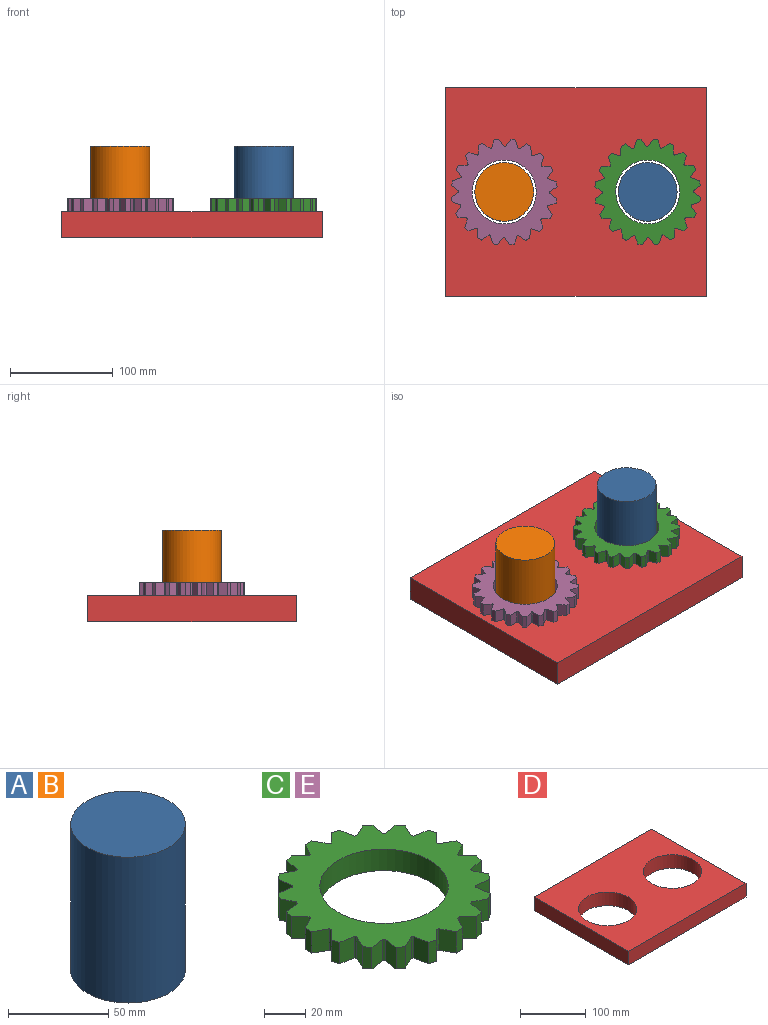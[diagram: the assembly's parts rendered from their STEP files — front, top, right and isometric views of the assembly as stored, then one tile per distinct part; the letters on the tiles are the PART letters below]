
ASSEMBLY  parts=5 mates=4
PART A: 3 faces, bbox 57.2x57.2x88.9 mm
  f0: cylinder r=28.57mm len=88.9mm, axis (0,0,-1), area 15961.3mm2, adj f1,f2
  f1: plane 57.15x57.15mm, normal (0,0,1), area 2565.2mm2, adj f0
  f2: plane 57.15x57.15mm, normal (0,0,-1), area 2565.2mm2, adj f0
PART B: same geometry as A
PART C: 83 faces, bbox 103.2x103.2x12.7 mm
  f0: plane 12.7x7.62mm, normal (0.47,0.88,0), area 109.7mm2, adj f1,f79,f81,f82
  f1: cylinder r=44.45mm len=12.7mm, axis (0,0,-1), area 15.5mm2, adj f0,f2,f81,f82
  f2: plane 12.7x6.21mm, normal (0.72,-0.69,0), area 109.6mm2, adj f1,f3,f81,f82
  f3: plane 12.7x4.35mm, normal (0.95,0.31,0), area 58.1mm2, adj f2,f4,f81,f82
  f4: plane 12.7x8.51mm, normal (0.18,0.98,0), area 109.7mm2, adj f3,f5,f81,f82
  f5: cylinder r=44.45mm len=12.7mm, axis (0,0,-1), area 15.5mm2, adj f4,f6,f81,f82
  f6: plane 12.7x7.76mm, normal (0.9,-0.44,0), area 109.6mm2, adj f5,f7,f81,f82
  f7: plane 12.7x3.7mm, normal (0.81,0.59,0), area 58.1mm2, adj f6,f8,f81,f82
  f8: plane 12.7x8.56mm, normal (-0.14,0.99,0), area 109.7mm2, adj f7,f9,f81,f82
  f9: cylinder r=44.45mm len=12.7mm, axis (0,0,-1), area 15.5mm2, adj f8,f10,f81,f82
  f10: plane 12.7x8.55mm, normal (0.99,-0.14,0), area 109.6mm2, adj f9,f11,f81,f82
  f11: plane 12.7x3.7mm, normal (0.59,0.81,0), area 58.1mm2, adj f10,f12,f81,f82
  f12: plane 12.7x7.77mm, normal (-0.44,0.9,0), area 109.7mm2, adj f11,f13,f81,f82
  f13: cylinder r=44.45mm len=12.7mm, axis (0,0,-1), area 15.5mm2, adj f12,f14,f81,f82
  f14: plane 12.7x8.5mm, normal (0.98,0.17,0), area 109.6mm2, adj f13,f15,f81,f82
  f15: plane 12.7x4.35mm, normal (0.31,0.95,0), area 58.1mm2, adj f14,f16,f81,f82
  f16: plane 12.7x6.23mm, normal (-0.69,0.72,0), area 109.7mm2, adj f15,f17,f81,f82
  f17: cylinder r=44.45mm len=12.7mm, axis (0,0,-1), area 15.5mm2, adj f16,f18,f81,f82
  f18: plane 12.7x7.62mm, normal (0.88,0.47,0), area 109.6mm2, adj f17,f19,f81,f82
  f19: plane 12.7x4.57mm, normal (0,1,0), area 58.1mm2, adj f18,f20,f81,f82
  f20: plane 12.7x7.62mm, normal (-0.88,0.47,0), area 109.7mm2, adj f19,f21,f81,f82
  f21: cylinder r=44.45mm len=12.7mm, axis (0,0,-1), area 15.5mm2, adj f20,f22,f81,f82
  f22: plane 12.7x6.21mm, normal (0.69,0.72,0), area 109.6mm2, adj f21,f23,f81,f82
  f23: plane 12.7x4.35mm, normal (-0.31,0.95,0), area 58.1mm2, adj f22,f24,f81,f82
  f24: plane 12.7x8.51mm, normal (-0.98,0.18,0), area 109.7mm2, adj f23,f25,f81,f82
  f25: cylinder r=44.45mm len=12.7mm, axis (0,0,-1), area 15.5mm2, adj f24,f26,f81,f82
  f26: plane 12.7x7.76mm, normal (0.44,0.9,0), area 109.6mm2, adj f25,f27,f81,f82
  f27: plane 12.7x3.7mm, normal (-0.59,0.81,0), area 58.1mm2, adj f26,f28,f81,f82
  f28: plane 12.7x8.56mm, normal (-0.99,-0.14,0), area 109.7mm2, adj f27,f29,f81,f82
  f29: cylinder r=44.45mm len=12.7mm, axis (0,0,-1), area 15.5mm2, adj f28,f30,f81,f82
  f30: plane 12.7x8.55mm, normal (0.14,0.99,0), area 109.6mm2, adj f29,f31,f81,f82
  f31: plane 12.7x3.7mm, normal (-0.81,0.59,0), area 58.1mm2, adj f30,f32,f81,f82
  f32: plane 12.7x7.77mm, normal (-0.9,-0.44,0), area 109.7mm2, adj f31,f33,f81,f82
  f33: cylinder r=44.45mm len=12.7mm, axis (0,0,-1), area 15.5mm2, adj f32,f34,f81,f82
  f34: plane 12.7x8.5mm, normal (-0.17,0.98,0), area 109.6mm2, adj f33,f35,f81,f82
  f35: plane 12.7x4.35mm, normal (-0.95,0.31,0), area 58.1mm2, adj f34,f36,f81,f82
  f36: plane 12.7x6.23mm, normal (-0.72,-0.69,0), area 109.7mm2, adj f35,f37,f81,f82
  f37: cylinder r=44.45mm len=12.7mm, axis (0,0,-1), area 15.5mm2, adj f36,f38,f81,f82
  f38: plane 12.7x7.62mm, normal (-0.47,0.88,0), area 109.6mm2, adj f37,f39,f81,f82
  f39: plane 12.7x4.57mm, normal (-1,0,0), area 58.1mm2, adj f38,f40,f81,f82
  f40: plane 12.7x7.62mm, normal (-0.47,-0.88,0), area 109.7mm2, adj f39,f41,f81,f82
  f41: cylinder r=44.45mm len=12.7mm, axis (0,0,-1), area 15.5mm2, adj f40,f42,f81,f82
  f42: plane 12.7x6.21mm, normal (-0.72,0.69,0), area 109.6mm2, adj f41,f43,f81,f82
  f43: plane 12.7x4.35mm, normal (-0.95,-0.31,0), area 58.1mm2, adj f42,f44,f81,f82
  f44: plane 12.7x8.51mm, normal (-0.18,-0.98,0), area 109.7mm2, adj f43,f45,f81,f82
  f45: cylinder r=44.45mm len=12.7mm, axis (0,0,-1), area 15.5mm2, adj f44,f46,f81,f82
  f46: plane 12.7x7.76mm, normal (-0.9,0.44,0), area 109.6mm2, adj f45,f47,f81,f82
  f47: plane 12.7x3.7mm, normal (-0.81,-0.59,0), area 58.1mm2, adj f46,f48,f81,f82
  f48: plane 12.7x8.56mm, normal (0.14,-0.99,0), area 109.7mm2, adj f47,f49,f81,f82
  f49: cylinder r=44.45mm len=12.7mm, axis (0,0,-1), area 15.5mm2, adj f48,f50,f81,f82
  f50: plane 12.7x8.55mm, normal (-0.99,0.14,0), area 109.6mm2, adj f49,f51,f81,f82
  f51: plane 12.7x3.7mm, normal (-0.59,-0.81,0), area 58.1mm2, adj f50,f52,f81,f82
  f52: plane 12.7x7.77mm, normal (0.44,-0.9,0), area 109.7mm2, adj f51,f53,f81,f82
  f53: cylinder r=44.45mm len=12.7mm, axis (0,0,-1), area 15.5mm2, adj f52,f54,f81,f82
  f54: plane 12.7x8.5mm, normal (-0.98,-0.17,0), area 109.6mm2, adj f53,f55,f81,f82
  f55: plane 12.7x4.35mm, normal (-0.31,-0.95,0), area 58.1mm2, adj f54,f56,f81,f82
  f56: plane 12.7x6.23mm, normal (0.69,-0.72,0), area 109.7mm2, adj f55,f57,f81,f82
  f57: cylinder r=44.45mm len=12.7mm, axis (0,0,-1), area 15.5mm2, adj f56,f58,f81,f82
  f58: plane 12.7x7.62mm, normal (-0.88,-0.47,0), area 109.6mm2, adj f57,f59,f81,f82
  f59: plane 12.7x4.57mm, normal (0,-1,0), area 58.1mm2, adj f58,f60,f81,f82
  f60: plane 12.7x7.62mm, normal (0.88,-0.47,0), area 109.7mm2, adj f59,f61,f81,f82
  f61: cylinder r=44.45mm len=12.7mm, axis (0,0,-1), area 15.5mm2, adj f60,f62,f81,f82
  f62: plane 12.7x6.21mm, normal (-0.69,-0.72,0), area 109.6mm2, adj f61,f63,f81,f82
  f63: plane 12.7x4.35mm, normal (0.31,-0.95,0), area 58.1mm2, adj f62,f64,f81,f82
  f64: plane 12.7x8.51mm, normal (0.98,-0.18,0), area 109.7mm2, adj f63,f65,f81,f82
  f65: cylinder r=44.45mm len=12.7mm, axis (0,0,-1), area 15.5mm2, adj f64,f66,f81,f82
  f66: plane 12.7x7.76mm, normal (-0.44,-0.9,0), area 109.6mm2, adj f65,f67,f81,f82
  f67: plane 12.7x3.7mm, normal (0.59,-0.81,0), area 58.1mm2, adj f66,f68,f81,f82
  f68: plane 12.7x8.56mm, normal (0.99,0.14,0), area 109.7mm2, adj f67,f69,f81,f82
  f69: cylinder r=44.45mm len=12.7mm, axis (0,0,-1), area 15.5mm2, adj f68,f70,f81,f82
  f70: plane 12.7x8.55mm, normal (-0.14,-0.99,0), area 109.6mm2, adj f69,f71,f81,f82
  f71: plane 12.7x3.7mm, normal (0.81,-0.59,0), area 58.1mm2, adj f70,f72,f81,f82
  f72: plane 12.7x7.77mm, normal (0.9,0.44,0), area 109.7mm2, adj f71,f73,f81,f82
  f73: cylinder r=44.45mm len=12.7mm, axis (0,0,-1), area 15.5mm2, adj f72,f74,f81,f82
  f74: plane 12.7x8.5mm, normal (0.17,-0.98,0), area 109.6mm2, adj f73,f75,f81,f82
  f75: plane 12.7x4.35mm, normal (0.95,-0.31,0), area 58.1mm2, adj f74,f76,f81,f82
  f76: plane 12.7x6.23mm, normal (0.72,0.69,0), area 109.7mm2, adj f75,f77,f81,f82
  f77: cylinder r=44.45mm len=12.7mm, axis (0,0,-1), area 15.5mm2, adj f76,f78,f81,f82
  f78: plane 12.7x7.62mm, normal (0.47,-0.88,0), area 109.6mm2, adj f77,f79,f81,f82
  f79: plane 12.7x4.57mm, normal (1,0,0), area 58.1mm2, adj f0,f78,f81,f82
  f80: cylinder r=31.12mm len=62.23mm, axis (0,0,-1), area 2482.9mm2, adj f81,f82
  f81: plane 103.22x103.22mm, normal (0,0,1), area 4404.2mm2, adj f0,f1,f2,f3,f4,f5,f6,f7
  f82: plane 103.22x103.22mm, normal (0,0,-1), area 4404.2mm2, adj f0,f1,f2,f3,f4,f5,f6,f7
PART D: 8 faces, bbox 254x203.2x25.4 mm
  f0: plane 203.2x25.4mm, normal (-1,0,0), area 5161.3mm2, adj f1,f4,f6,f7
  f1: plane 254x25.4mm, normal (0,-1,0), area 6451.6mm2, adj f0,f2,f6,f7
  f2: plane 203.2x25.4mm, normal (1,0,0), area 5161.3mm2, adj f1,f4,f6,f7
  f3: cylinder r=44.45mm len=88.9mm, axis (0,0,-1), area 7093.9mm2, adj f6,f7
  f4: plane 254x25.4mm, normal (0,1,0), area 6451.6mm2, adj f0,f2,f6,f7
  f5: cylinder r=44.45mm len=88.9mm, axis (0,0,-1), area 7093.9mm2, adj f6,f7
  f6: plane 254x203.2mm, normal (0,0,1), area 39198.5mm2, adj f0,f1,f2,f3,f4,f5
  f7: plane 254x203.2mm, normal (0,0,-1), area 39198.5mm2, adj f0,f1,f2,f3,f4,f5
PART E: same geometry as C
PLACE A rot(axis=(0.49,-0.87,0),180deg) t=(196.85,101.6,88.9)mm fixed
PLACE B t=(57.15,101.6,0)mm fixed
PLACE C rot(axis=(0,0,1),117.7deg) t=(196.85,101.6,25.4)mm
PLACE D at identity
PLACE E rot(axis=(0,0,-1),117.7deg) t=(57.15,101.6,25.4)mm
MATE revolute B.f0 <-> D.f3  axis (0,0,-1) through (57.15,101.6,0)mm
MATE revolute D.f5 <-> A.f0  axis (0,0,-1) through (196.85,101.6,0)mm
MATE revolute C.f80 <-> D.f5  axis (0,0,-1) through (196.85,101.6,25.4)mm
MATE revolute E.f80 <-> D.f3  axis (0,0,-1) through (57.15,101.6,25.4)mm
